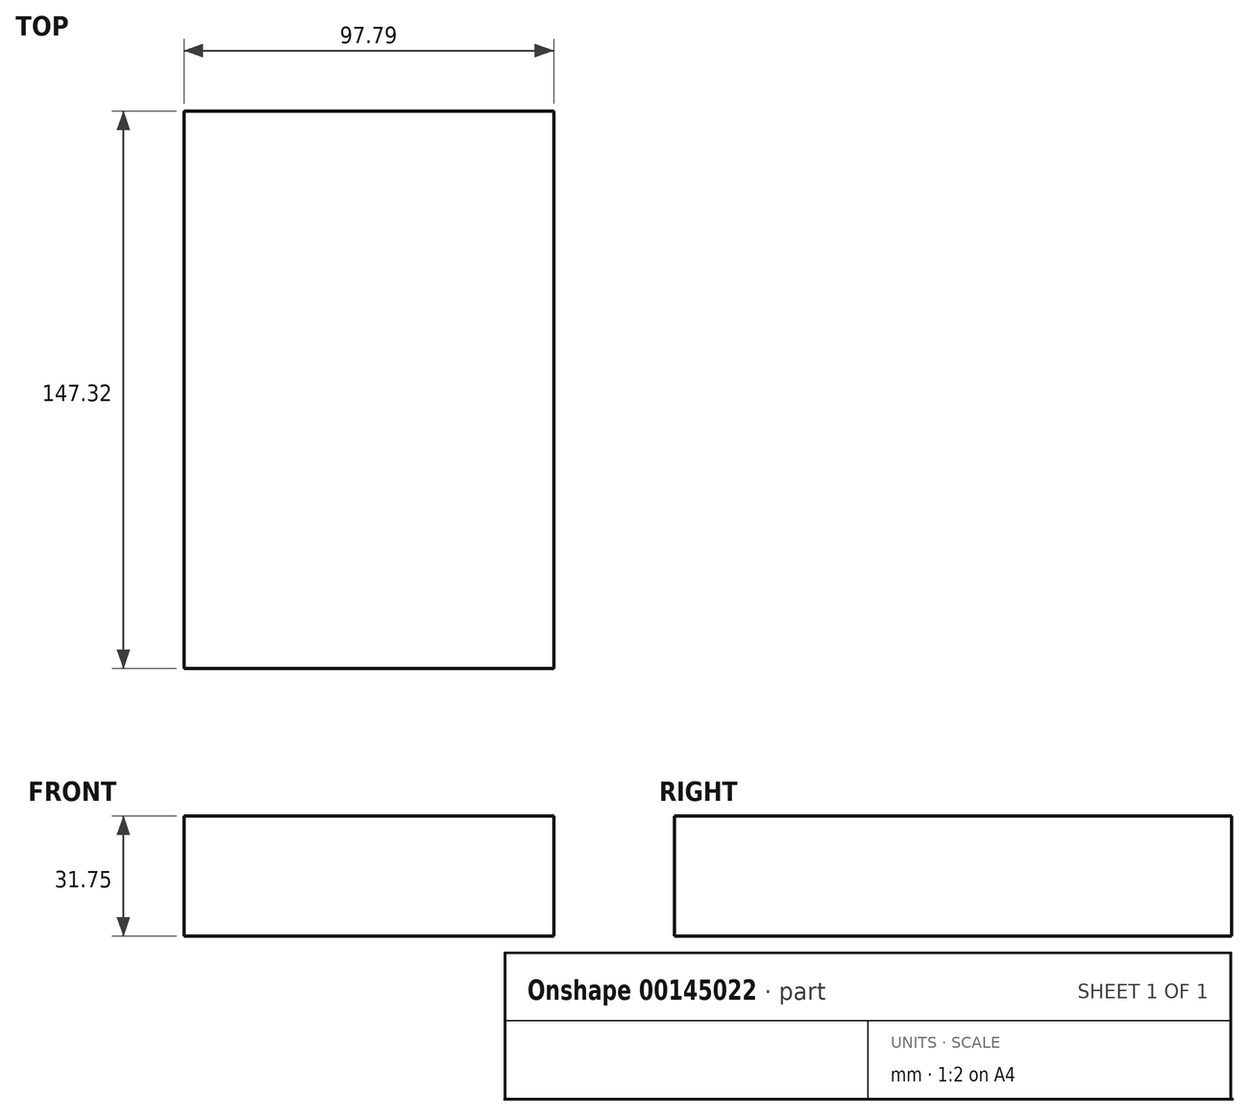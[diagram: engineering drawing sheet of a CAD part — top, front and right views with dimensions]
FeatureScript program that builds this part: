
annotation { "Feature Type Name" : "Feature", "Feature Type Description" : "" }
export const myFeature = defineFeature(function(context is Context, id is Id, definition is map)
    precondition{}
    {
        {
            var Q0;
            Q0=qCreatedBy(makeId("Front.planeOp"),FACE);
            var sketch = newSketch(context, id + "F0", { "sketchPlane" : qUnion([Q0])});
            skLineSegment(sketch, "E0.bottom", {"start": v(-44.34, 0) * mm, "end": v(53.45, 0) * mm});
            skLineSegment(sketch, "E0.top", {"start": v(-44.34, 31.75) * mm, "end": v(53.45, 31.75) * mm});
            skLineSegment(sketch, "E0.left", {"start": v(-44.34, 0) * mm, "end": v(-44.34, 31.75) * mm});
            skLineSegment(sketch, "E0.right", {"start": v(53.45, 0) * mm, "end": v(53.45, 31.75) * mm});
            skSolve(sketch);
        }
        {
            var Q0;
            Q0=makeQuery(id+"F0.imprint","IMPRINT",FACE,{"disambiguationData":[TD([[makeQuery(id+"F0.imprint","IMPRINT",EDGE,{"derivedFrom":sQuery(id+"F0.wireOp",EDGE,"E0.bottom")}),1.0]])]});
            extrude(context, id + "F1", {"entities" : qUnion([Q0]), "depth" : 147.32 * mm});
        }
    });
